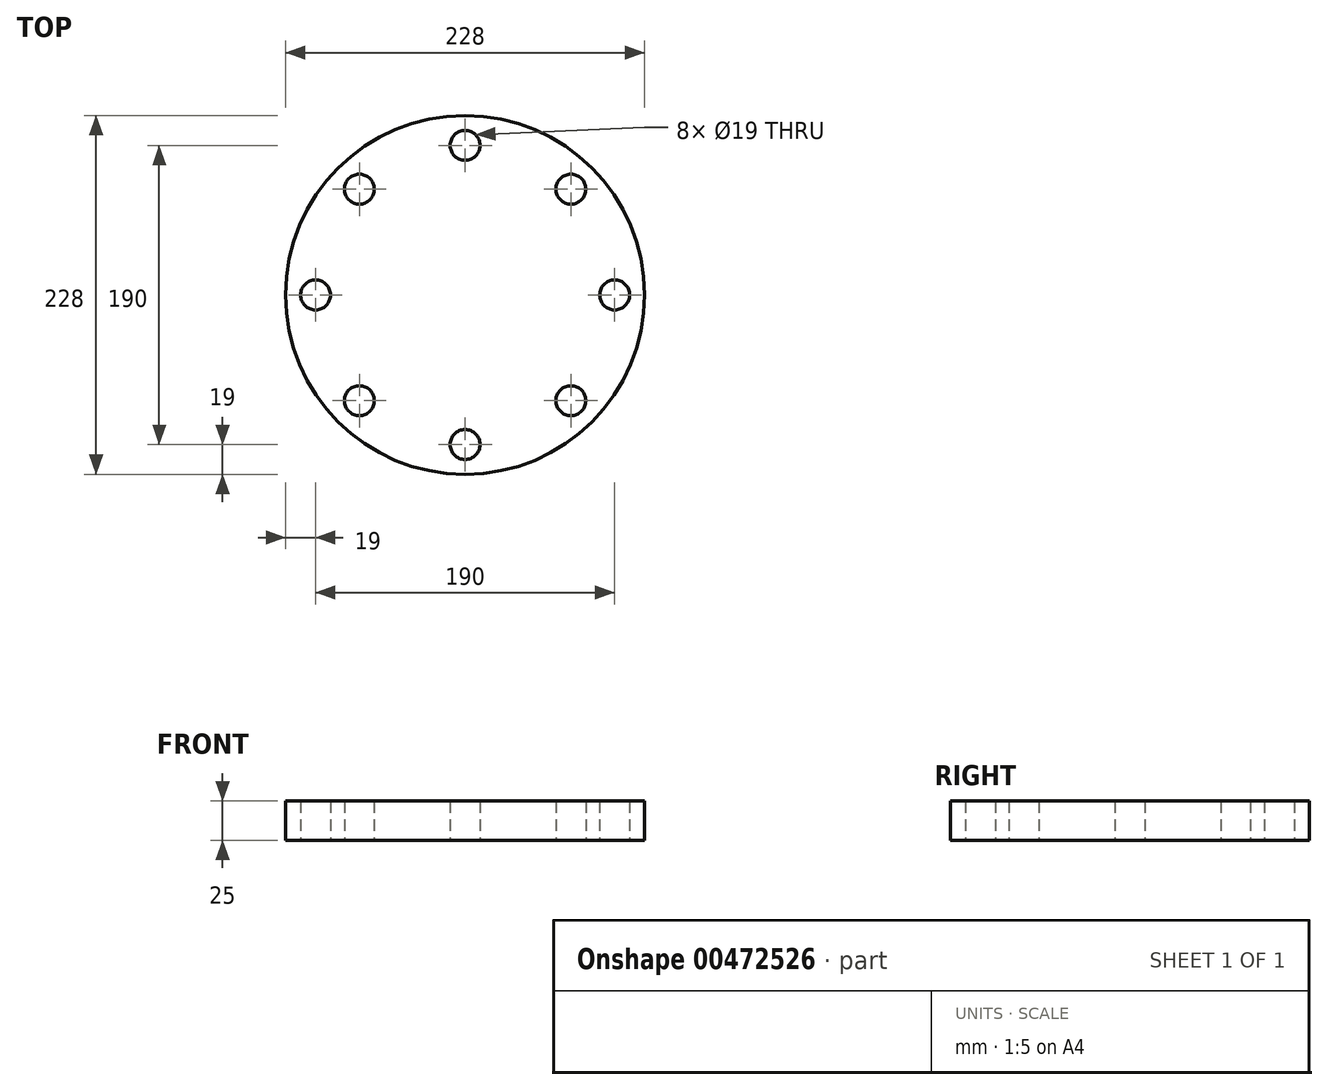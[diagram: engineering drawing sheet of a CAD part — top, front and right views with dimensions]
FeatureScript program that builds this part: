
annotation { "Feature Type Name" : "Feature", "Feature Type Description" : "" }
export const myFeature = defineFeature(function(context is Context, id is Id, definition is map)
    precondition{}
    {
        {
            var Q0;
            Q0=qCreatedBy(makeId("Top.planeOp"),FACE);
            var sketch = newSketch(context, id + "F0", { "sketchPlane" : qUnion([Q0])});
            skCircle(sketch, "E0", {"center": v(0, 0) * mm, "radius": 114 * mm});
            skCircle(sketch, "E1", {"center": v(95, 0) * mm, "radius": 9.5 * mm});
            skCircle(sketch, "E2.1.0", {"center": v(67.18, 67.18) * mm, "radius": 9.5 * mm});
            skCircle(sketch, "E2.2.0", {"center": v(0, 95) * mm, "radius": 9.5 * mm});
            skCircle(sketch, "E2.3.0", {"center": v(-67.18, 67.18) * mm, "radius": 9.5 * mm});
            skCircle(sketch, "E2.4.0", {"center": v(-95, 0) * mm, "radius": 9.5 * mm});
            skCircle(sketch, "E2.5.0", {"center": v(-67.18, -67.18) * mm, "radius": 9.5 * mm});
            skCircle(sketch, "E2.6.0", {"center": v(0, -95) * mm, "radius": 9.5 * mm});
            skCircle(sketch, "E2.7.0", {"center": v(67.18, -67.18) * mm, "radius": 9.5 * mm});
            skSolve(sketch);
        }
        {
            var Q0;
            Q0 = qSketchRegion(id + "F0", true);
            extrude(context, id + "F1", {"entities" : qUnion([Q0]), "depth" : 25 * mm});
        }
    });
